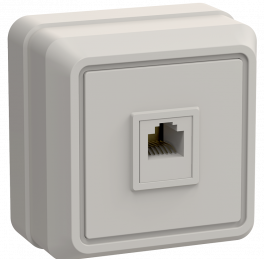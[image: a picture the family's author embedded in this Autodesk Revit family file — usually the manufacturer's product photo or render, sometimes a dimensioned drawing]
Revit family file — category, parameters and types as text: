
# Revit family: IEK_РозеткаТелефонная_ОткрытойУстановки_1-местная IP20_ОКТАВА
name_source: partatom
category: Устройства связи
units: mm (PartAtom-declared; Revit-internal decimal feet)

## family parameters
Всегда вертикально = Да
На основе рабочей плоскости = Нет
Общий = Нет
При загрузке вырезать с полостями = Нет
Размер круглого соединителя = Использовать диаметр
Сохранять ориентацию аннотаций = Да
Тип детали = Нормальный
Точка расчета площади = Нет

## types (1)
- РТ20-ОКм
    ADSK_URL страницы изделия = https://www.iek.ru
    ADSK_Версия Revit = 2019
    ADSK_Версия семейства = 1.0
    ADSK_Группирование = III ЭЛЕКТРОУСТАНОВОЧНЫЕ И ЭЛЕКТРОМОНТАЖНЫЕ ИЗДЕЛИЯ
    ADSK_Единица измерения = шт
    ADSK_Завод-изготовитель = IEK
    ADSK_Код изделия = ETO10-K33-DC
    ADSK_Марка = ОКТАВА
    ADSK_Масса = 0.048
    ADSK_Материал = Цвет кремовый
    ADSK_Материал наименование = Пластик
    ADSK_Наименование = Розетка 1-местная для открытой установки телефонная РТ20-ОКм ОКТАВА кремовый IEK
    IEK_URL = https://www.iek.ru
    IEK_Описание = Универсальный дизайн серии открытой установки "ОКТАВА" позволяет устанавливать изделия в квартирах, загородных домах, офисных и производственных помещениях.
    IEK_Цена за единицу = 132.29
    KSI_CMa_Строительные материалы = 01.7.14.03
    Высота = 61 мм
    Глубина = 37 мм
    Изготовитель = IEK
    Степень защиты = IP20
    Тип монтажа = Поверхность монтажа (открытая установка)
    Ширина = 61 мм
